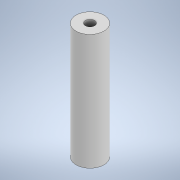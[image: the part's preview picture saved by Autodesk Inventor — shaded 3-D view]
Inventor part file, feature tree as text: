
AUTODESK INVENTOR PART (.ipt)
format: ipt  version: 2022 (Build 260153000, 153)  size: 94,720 bytes
history: native  units: mm
features: extrude x1, sketch x1
ambient origin geometry x8: Origin, YZ Plane, XZ Plane, XY Plane, X Axis, Y Axis, Z Axis, Center Point
bodies: Solid1 (feature_tree)
feature tree (2):
  extrude  "Extrusion1"  Depth=25.0mm
  sketch  "Sketch1"  dims[d0=2.0mm d1=6.0mm d2=25.0mm d3=0.0mm]
